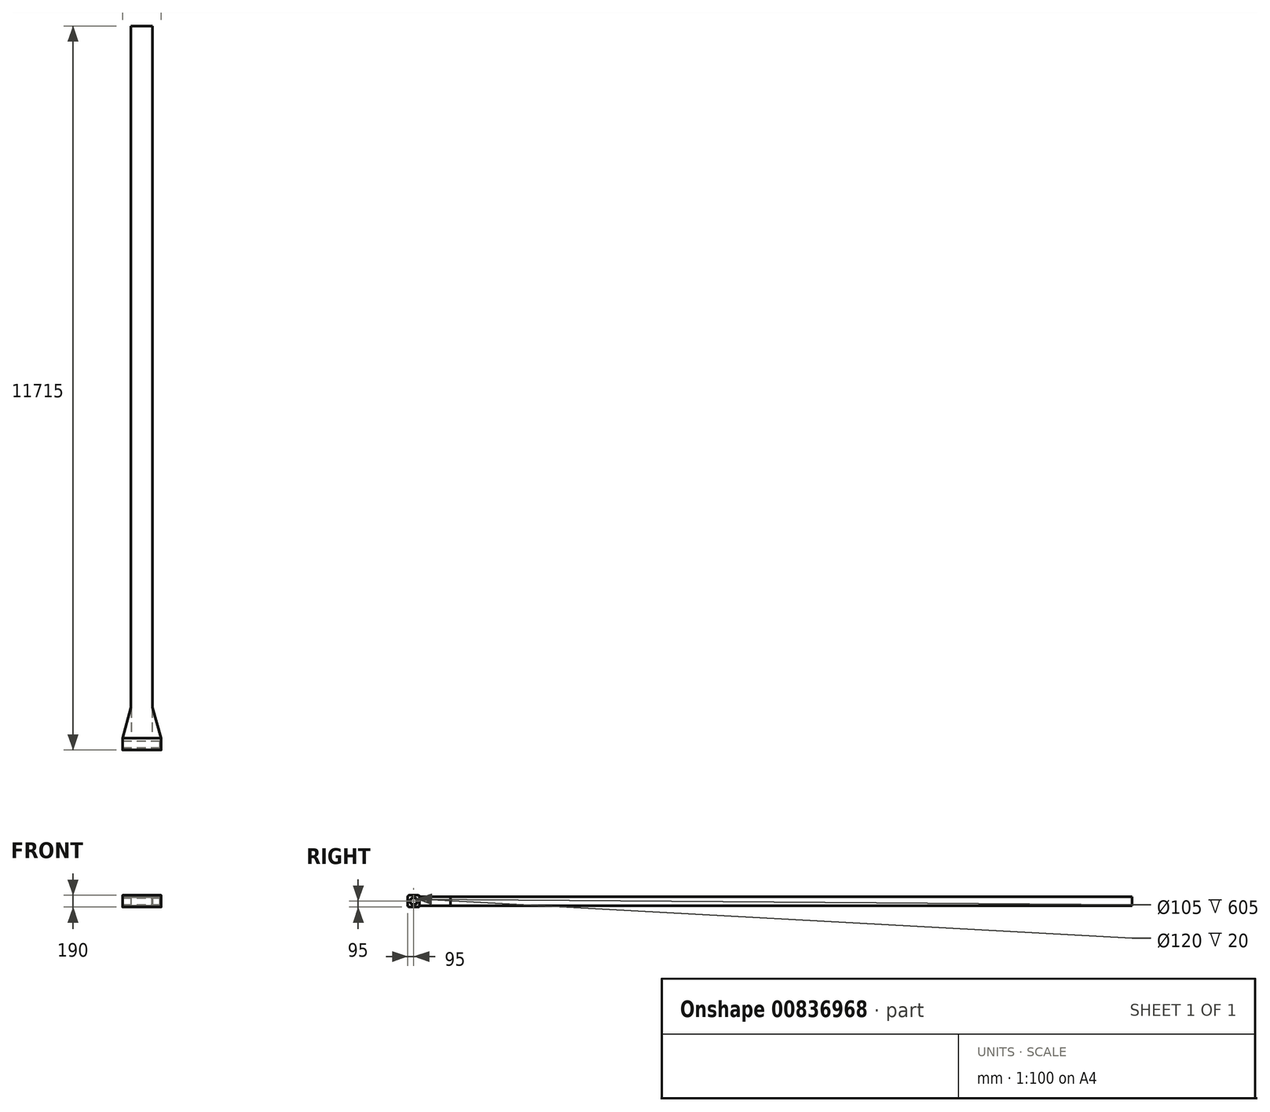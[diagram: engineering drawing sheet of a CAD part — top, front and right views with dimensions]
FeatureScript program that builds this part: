
annotation { "Feature Type Name" : "Feature", "Feature Type Description" : "" }
export const myFeature = defineFeature(function(context is Context, id is Id, definition is map)
    precondition{}
    {
        {
            var Q0;
            Q0=qCreatedBy(makeId("Right.planeOp"),FACE);
            var sketch = newSketch(context, id + "F0", { "sketchPlane" : qUnion([Q0])});
            skCircle(sketch, "E0", {"center": v(0, 0) * mm, "radius": 60 * mm});
            skLineSegment(sketch, "E1.bottom", {"start": v(-75, 95) * mm, "end": v(75, 95) * mm});
            skLineSegment(sketch, "E1.top", {"start": v(-75, -95) * mm, "end": v(75, -95) * mm});
            skLineSegment(sketch, "E1.left", {"start": v(-95, 75) * mm, "end": v(-95, -75) * mm});
            skLineSegment(sketch, "E1.right", {"start": v(95, 75) * mm, "end": v(95, -75) * mm});
            skCircle(sketch, "E2", {"center": v(0, 0) * mm, "radius": 53.03 * mm});
            skPoint(sketch, "E3.visualSharp", {"position": v(95, 95) * mm});
            skArc(sketch, "E3.filletArc", {"start": v(95, 75) * mm, "mid": v(89.14, 89.14) * mm, "end": v(75, 95) * mm});
            skPoint(sketch, "E4.visualSharp", {"position": v(-95, 95) * mm});
            skArc(sketch, "E4.filletArc", {"start": v(-75, 95) * mm, "mid": v(-89.14, 89.14) * mm, "end": v(-95, 75) * mm});
            skPoint(sketch, "E5.visualSharp", {"position": v(95, -95) * mm});
            skArc(sketch, "E5.filletArc", {"start": v(75, -95) * mm, "mid": v(89.14, -89.14) * mm, "end": v(95, -75) * mm});
            skPoint(sketch, "E6.visualSharp", {"position": v(-95, -95) * mm});
            skArc(sketch, "E6.filletArc", {"start": v(-95, -75) * mm, "mid": v(-89.14, -89.14) * mm, "end": v(-75, -95) * mm});
            skLineSegment(sketch, "E7", {"start": v(-120, 0) * mm, "end": v(-120, 75) * mm});
            skLineSegment(sketch, "E8", {"start": v(-120, 75) * mm, "end": v(-95, 75) * mm});
            skLineSegment(sketch, "E9.MirrorCS", {"start": v(-120, 0) * mm, "end": v(-120, -75) * mm});
            skLineSegment(sketch, "E10.MirrorCS", {"start": v(-120, -75) * mm, "end": v(-95, -75) * mm});
            skSolve(sketch);
        }
        {
            var Q0;
            Q0=makeQuery(id+"F0.imprint","IMPRINT",FACE,{"disambiguationData":[TD([[makeQuery(id+"F0.imprint","IMPRINT",EDGE,{"derivedFrom":sQuery(id+"F0.wireOp",EDGE,"E0")}),-1.0]])]});
            var Q1;
            Q1=makeQuery(id+"F0.imprint","IMPRINT",FACE,{"disambiguationData":[TD([[makeQuery(id+"F0.imprint","IMPRINT",EDGE,{"derivedFrom":sQuery(id+"F0.wireOp",EDGE,"E0")}),1.0]])]});
            var Q2;
            Q2=makeQuery(id+"F0.imprint","IMPRINT",FACE,{"disambiguationData":[TD([[makeQuery(id+"F0.imprint","IMPRINT",EDGE,{"derivedFrom":sQuery(id+"F0.wireOp",EDGE,"E2")}),1.0]])]});
            extrude(context, id + "F1", {"entities" : qUnion([Q0, Q1, Q2]), "endBound" : BoundingType.SYMMETRIC, "depth" : 625 * mm, "offsetDistance" : 25 * mm});
        }
        {
            var Q0;
            Q0=makeQuery(id+"F1.opExtrude","CAP_FACE",FACE,{"disambiguationData":[OSD([sQuery(id+"F0.wireOp",EDGE,"E1.bottom"),sQuery(id+"F0.wireOp",EDGE,"E1.top"),sQuery(id+"F0.wireOp",EDGE,"E1.left"),sQuery(id+"F0.wireOp",EDGE,"E1.right"),sQuery(id+"F0.wireOp",EDGE,"E3.filletArc"),sQuery(id+"F0.wireOp",EDGE,"E4.filletArc"),sQuery(id+"F0.wireOp",EDGE,"E5.filletArc"),sQuery(id+"F0.wireOp",EDGE,"E6.filletArc")])],"isStart":false});
            var sketch = newSketch(context, id + "F2", { "sketchPlane" : qUnion([Q0])});
            skCircle(sketch, "E11", {"center": v(0, 0) * mm, "radius": 60 * mm});
            skCircle(sketch, "E12", {"center": v(0, 0) * mm, "radius": 52.5 * mm});
            skSolve(sketch);
        }
        {
            var Q0;
            Q0=makeQuery(id+"F2.imprint","IMPRINT",FACE,{"disambiguationData":[TD([[makeQuery(id+"F2.imprint","IMPRINT",EDGE,{"derivedFrom":sQuery(id+"F2.wireOp",EDGE,"E12")}),1.0]])]});
            extrude(context, id + "F3", {"entities" : qUnion([Q0]), "operationType" : NewBodyOperationType.REMOVE, "endBound" : BoundingType.THROUGH_ALL, "oppositeDirection" : true, "depth" : 25 * mm, "offsetDistance" : 25 * mm});
        }
        {
            var Q0;
            Q0=makeQuery(id+"F2.imprint","IMPRINT",FACE,{"disambiguationData":[TD([[makeQuery(id+"F2.imprint","IMPRINT",EDGE,{"derivedFrom":sQuery(id+"F2.wireOp",EDGE,"E11")}),1.0]])]});
            extrude(context, id + "F4", {"entities" : qUnion([Q0]), "operationType" : NewBodyOperationType.REMOVE, "oppositeDirection" : true, "depth" : 20 * mm, "offsetDistance" : 25 * mm});
        }
        {
            var Q0;
            Q0=qCreatedBy(makeId("Top.planeOp"),FACE);
            var sketch = newSketch(context, id + "F5", { "sketchPlane" : qUnion([Q0])});
            skLineSegment(sketch, "E13.bottom", {"start": v(312.5, 95) * mm, "end": v(-312.5, 95) * mm});
            skLineSegment(sketch, "E13.top", {"start": v(312.5, -95) * mm, "end": v(-312.5, -95) * mm});
            skLineSegment(sketch, "E13.left", {"start": v(312.5, 95) * mm, "end": v(312.5, -95) * mm});
            skLineSegment(sketch, "E13.right", {"start": v(-312.5, 95) * mm, "end": v(-312.5, -95) * mm});
            skPoint(sketch, "E13.middle", {"position": v(0, 0) * mm});
            skCircle(sketch, "E14", {"center": v(0, 95) * mm, "radius": 500 * mm, "construction": true});
            skCircle(sketch, "E15", {"center": v(0, 0) * mm, "radius": 11620 * mm, "construction": true});
            skPoint(sketch, "E16.orphan", {"position": v(173.78, 13891.9) * mm});
            skLineSegment(sketch, "E17", {"start": v(0, 0) * mm, "end": v(0, 11620) * mm, "construction": true});
            skLineSegment(sketch, "E18", {"start": v(0, 595) * mm, "end": v(175, 595) * mm, "construction": true});
            skLineSegment(sketch, "E19.MirrorCS", {"start": v(0, 595) * mm, "end": v(-175, 595) * mm, "construction": true});
            skLineSegment(sketch, "E20", {"start": v(312.5, 95) * mm, "end": v(175, 595) * mm});
            skLineSegment(sketch, "E21.MirrorCS", {"start": v(-312.5, 95) * mm, "end": v(-175, 595) * mm});
            skLineSegment(sketch, "E22", {"start": v(0, 11620) * mm, "end": v(175, 11620) * mm});
            skLineSegment(sketch, "E23", {"start": v(175, 11620) * mm, "end": v(175, 595) * mm});
            skLineSegment(sketch, "E24.MirrorCS", {"start": v(0, 11620) * mm, "end": v(-175, 11620) * mm});
            skLineSegment(sketch, "E25.MirrorCS", {"start": v(-175, 11620) * mm, "end": v(-175, 595) * mm});
            skSolve(sketch);
        }
        {
            var Q0;
            Q0=makeQuery(id+"F5.imprint","IMPRINT",FACE,{"disambiguationData":[TD([[makeQuery(id+"F5.imprint","IMPRINT",EDGE,{"derivedFrom":sQuery(id+"F5.wireOp",EDGE,"E13.bottom")}),-1.0]])]});
            var Q1;
            Q1=makeQuery(id+"F5.imprint","IMPRINT",FACE,{"disambiguationData":[TD([[makeQuery(id+"F5.imprint","IMPRINT",EDGE,{"derivedFrom":sQuery(id+"F5.wireOp",EDGE,"E18")}),1.0]])]});
            extrude(context, id + "F6", {"entities" : qUnion([Q0, Q1]), "operationType" : NewBodyOperationType.ADD, "endBound" : BoundingType.SYMMETRIC, "depth" : 150 * mm, "offsetDistance" : 25 * mm});
        }
        {
            var Q0;
            Q0=qCreatedBy(makeId("Front.planeOp"),FACE);
            cPlane(context, id + "F7", {"entities" : qUnion([Q0]), "cplaneType" : CPlaneType.OFFSET, "offset" : 90 * mm, "oppositeDirection" : true, "width" : 150 * mm, "height" : 150 * mm});
        }
        {
            var Q0;
            Q0=qCreatedBy(id+"F7.planeOp",FACE);
            var sketch = newSketch(context, id + "F8", { "sketchPlane" : qUnion([Q0])});
            skLineSegment(sketch, "E26.bottom", {"start": v(-175, 75) * mm, "end": v(175, 75) * mm});
            skLineSegment(sketch, "E26.top", {"start": v(-175, -75) * mm, "end": v(175, -75) * mm});
            skLineSegment(sketch, "E26.left", {"start": v(-175, 75) * mm, "end": v(-175, -75) * mm});
            skLineSegment(sketch, "E26.right", {"start": v(175, 75) * mm, "end": v(175, -75) * mm});
            skPoint(sketch, "E26.middle", {"position": v(0, 0) * mm});
            skLineSegment(sketch, "E27.bottom", {"start": v(167.5, 67.5) * mm, "end": v(-167.5, 67.5) * mm});
            skLineSegment(sketch, "E27.top", {"start": v(167.5, -67.5) * mm, "end": v(-167.5, -67.5) * mm});
            skLineSegment(sketch, "E27.left", {"start": v(167.5, 67.5) * mm, "end": v(167.5, -67.5) * mm});
            skLineSegment(sketch, "E27.right", {"start": v(-167.5, 67.5) * mm, "end": v(-167.5, -67.5) * mm});
            skSolve(sketch);
        }
        {
            var Q0;
            Q0=makeQuery(id+"F8.imprint","IMPRINT",FACE,{"disambiguationData":[TD([[makeQuery(id+"F8.imprint","IMPRINT",EDGE,{"derivedFrom":sQuery(id+"F8.wireOp",EDGE,"E27.bottom")}),1.0]])]});
            extrude(context, id + "F9", {"entities" : qUnion([Q0]), "operationType" : NewBodyOperationType.REMOVE, "endBound" : BoundingType.THROUGH_ALL, "oppositeDirection" : true, "depth" : 25 * mm, "offsetDistance" : 25 * mm});
        }
    });
